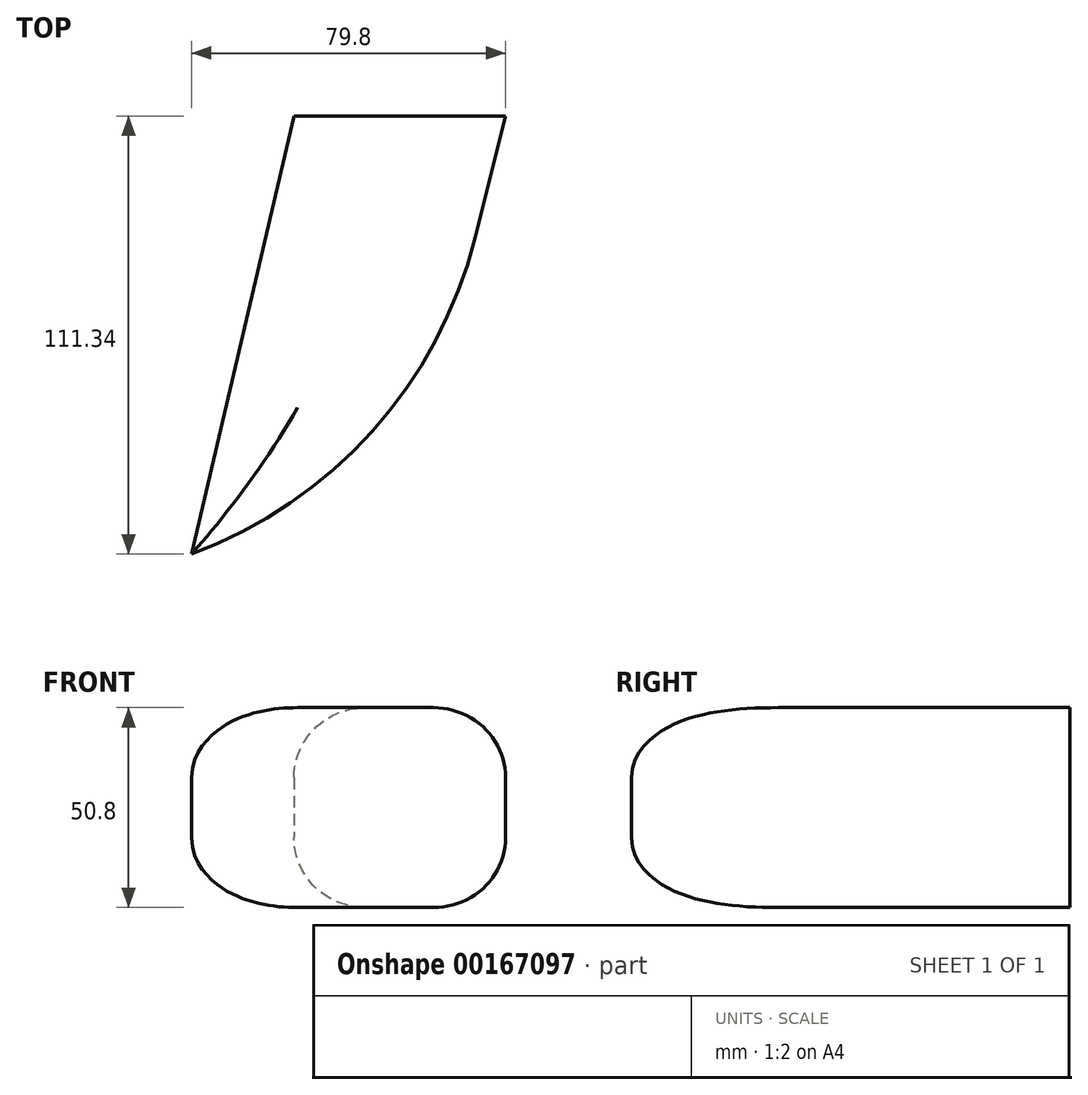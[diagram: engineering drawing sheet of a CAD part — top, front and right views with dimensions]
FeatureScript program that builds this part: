
annotation { "Feature Type Name" : "Feature", "Feature Type Description" : "" }
export const myFeature = defineFeature(function(context is Context, id is Id, definition is map)
    precondition{}
    {
        {
            var Q0;
            Q0=qCreatedBy(makeId("Top.planeOp"),FACE);
            var sketch = newSketch(context, id + "F0", { "sketchPlane" : qUnion([Q0])});
            skLineSegment(sketch, "E0", {"start": v(-50.57, 7.24) * mm, "end": v(3.23, 7.24) * mm});
            skLineSegment(sketch, "E1", {"start": v(-50.57, 7.24) * mm, "end": v(-76.57, -104.1) * mm});
            skLineSegment(sketch, "E2", {"start": v(3.23, 7.24) * mm, "end": v(-4.57, -23.78) * mm});
            skArc(sketch, "E3", {"start": v(-76.57, -104.1) * mm, "mid": v(-30.65, -72.83) * mm, "end": v(-4.57, -23.78) * mm});
            skSolve(sketch);
        }
        {
            var Q0;
            Q0=qSketchRegion(id+"F0",true);
            extrude(context, id + "F1", {"entities" : qUnion([Q0]), "depth" : 50.8 * mm});
        }
        {
            var Q0;
            Q0=makeQuery(id+"F1.opExtrude","CAP_EDGE",EDGE,{"disambiguationData":[OSD([sQuery(id+"F0.wireOp",EDGE,"C4H4PHbU-KKx9-q2EA-dDIi-FWc9RiPhfjej")])],"isStart":false});
            var Q1;
            Q1=makeQuery(id+"F1.opExtrude","CAP_EDGE",EDGE,{"disambiguationData":[OSD([sQuery(id+"F0.wireOp",EDGE,"E2")])],"isStart":false});
            var Q2;
            Q2=makeQuery(id+"F1.opExtrude","CAP_EDGE",EDGE,{"disambiguationData":[OSD([sQuery(id+"F0.wireOp",EDGE,"E1")])],"isStart":false});
            fillet(context, id + "F2", {"entities" : qUnion([Q0, Q1, Q2]), "radius" : 17.78 * mm, "tangentPropagation" : true, "allowEdgeOverflow" : false});
        }
        {
            var Q0;
            Q0=makeQuery(id+"F1.opExtrude","CAP_EDGE",EDGE,{"disambiguationData":[OSD([sQuery(id+"F0.wireOp",EDGE,"E2")])],"isStart":true});
            var Q1;
            Q1=makeQuery(id+"F1.opExtrude","CAP_EDGE",EDGE,{"disambiguationData":[OSD([sQuery(id+"F0.wireOp",EDGE,"C4H4PHbU-KKx9-q2EA-dDIi-FWc9RiPhfjej")])],"isStart":true});
            var Q2;
            Q2=makeQuery(id+"F1.opExtrude","CAP_EDGE",EDGE,{"disambiguationData":[OSD([sQuery(id+"F0.wireOp",EDGE,"E1")])],"isStart":true});
            fillet(context, id + "F3", {"entities" : qUnion([Q0, Q1, Q2]), "radius" : 17.78 * mm, "tangentPropagation" : true, "allowEdgeOverflow" : false});
        }
    });
